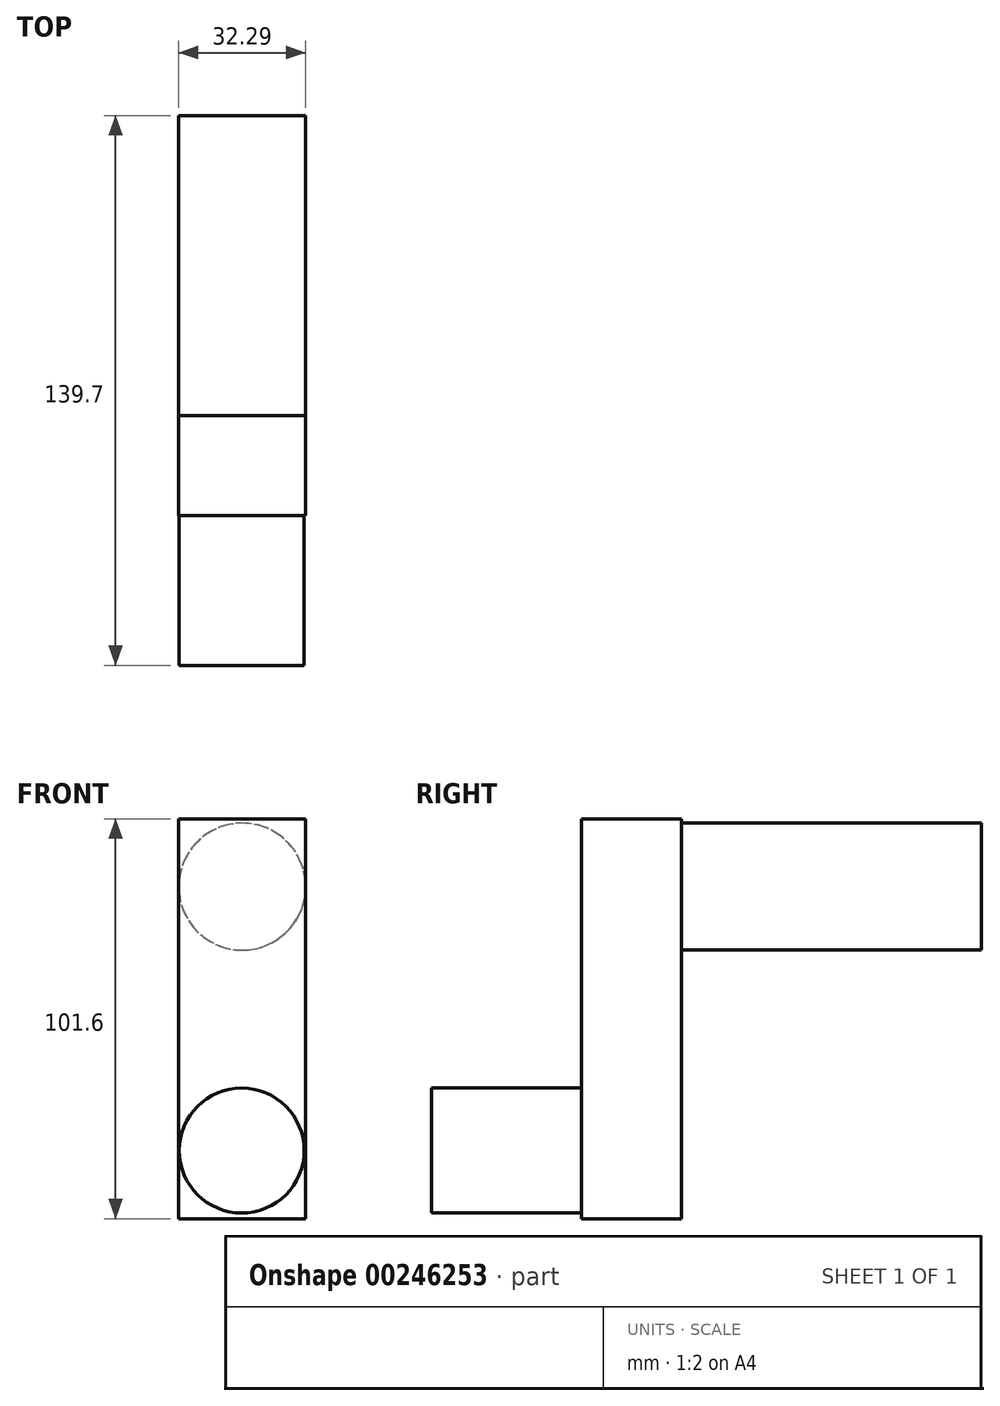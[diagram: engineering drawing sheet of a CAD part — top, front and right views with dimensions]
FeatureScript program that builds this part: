
annotation { "Feature Type Name" : "Feature", "Feature Type Description" : "" }
export const myFeature = defineFeature(function(context is Context, id is Id, definition is map)
    precondition{}
    {
        {
            var Q0;
            Q0=qCreatedBy(makeId("Front.planeOp"),FACE);
            var sketch = newSketch(context, id + "F0", { "sketchPlane" : qUnion([Q0])});
            skCircle(sketch, "E0", {"center": v(0, 0) * mm, "radius": 15.88 * mm});
            skSolve(sketch);
        }
        {
            var Q0;
            Q0=makeQuery(id+"F0.imprint","IMPRINT",FACE,{"disambiguationData":[TD([[makeQuery(id+"F0.imprint","IMPRINT",EDGE,{"derivedFrom":sQuery(id+"F0.wireOp",EDGE,"E0")}),1.0]])]});
            extrude(context, id + "F1", {"entities" : qUnion([Q0]), "depth" : 63.5 * mm});
        }
        {
            var Q0;
            Q0=qCreatedBy(makeId("Front.planeOp"),FACE);
            var sketch = newSketch(context, id + "F2", { "sketchPlane" : qUnion([Q0])});
            skLineSegment(sketch, "E1.bottom", {"start": v(16.24, 84.3) * mm, "end": v(-16.02, 84.3) * mm});
            skLineSegment(sketch, "E1.top", {"start": v(16.24, -17.3) * mm, "end": v(-16.02, -17.3) * mm});
            skLineSegment(sketch, "E1.left", {"start": v(16.24, 84.3) * mm, "end": v(16.24, -17.3) * mm});
            skLineSegment(sketch, "E1.right", {"start": v(-16.02, 84.3) * mm, "end": v(-16.02, -17.3) * mm});
            skSolve(sketch);
        }
        {
            var Q0;
            Q0 = qSketchRegion(id + "F2", true);
            extrude(context, id + "F3", {"entities" : qUnion([Q0]), "operationType" : NewBodyOperationType.ADD, "depth" : 25.4 * mm});
        }
        {
            var Q0;
            Q0=qCreatedBy(makeId("Front.planeOp"),FACE);
            var sketch = newSketch(context, id + "F4", { "sketchPlane" : qUnion([Q0])});
            skCircle(sketch, "E2", {"center": v(0.14, 67.05) * mm, "radius": 16.13 * mm});
            skSolve(sketch);
        }
        {
            var Q0;
            Q0 = qSketchRegion(id + "F4", true);
            extrude(context, id + "F5", {"entities" : qUnion([Q0]), "operationType" : NewBodyOperationType.ADD, "oppositeDirection" : true, "depth" : 76.2 * mm});
        }
    });
